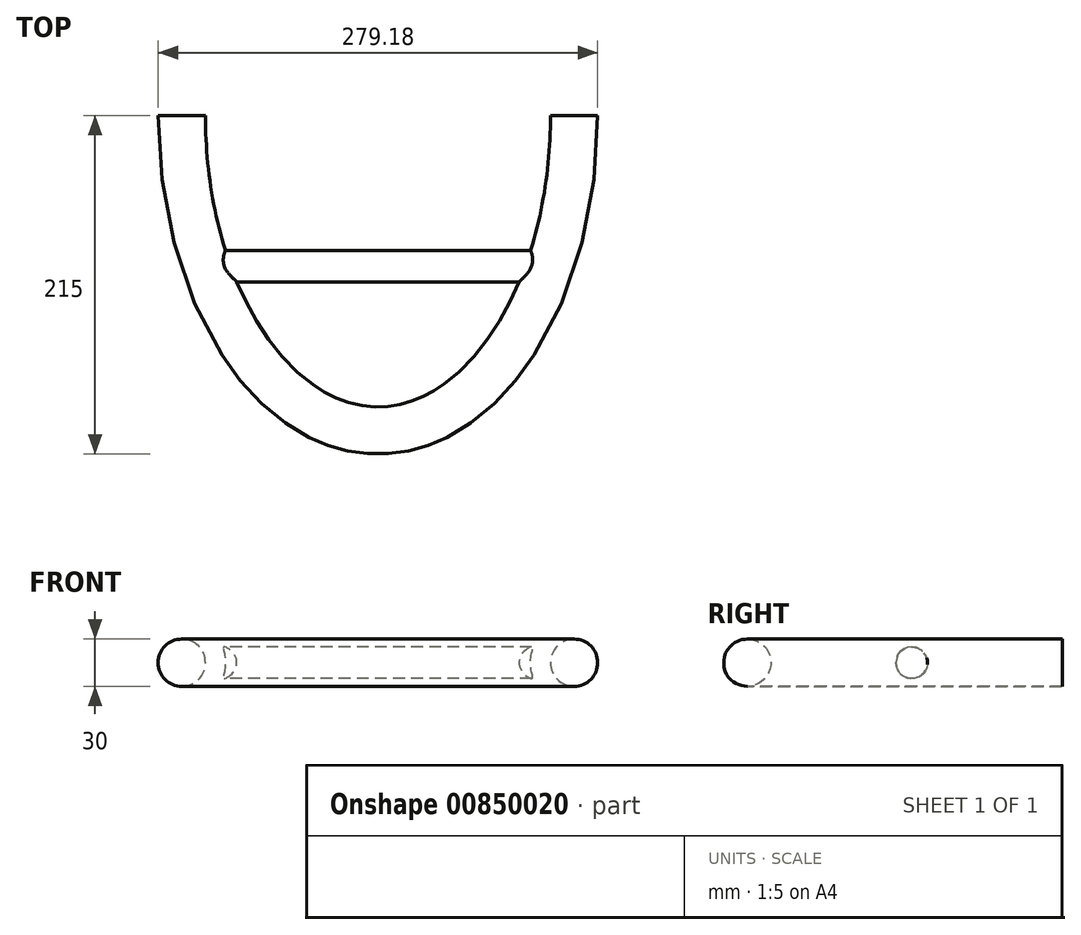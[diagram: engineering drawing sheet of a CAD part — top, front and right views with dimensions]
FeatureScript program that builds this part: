
annotation { "Feature Type Name" : "Feature", "Feature Type Description" : "" }
export const myFeature = defineFeature(function(context is Context, id is Id, definition is map)
    precondition{}
    {
        {
            var Q0;
            Q0=qCreatedBy(makeId("Front.planeOp"),FACE);
            var sketch = newSketch(context, id + "F0", { "sketchPlane" : qUnion([Q0])});
            skCircle(sketch, "E0", {"center": v(0, 0) * mm, "radius": 15 * mm});
            skSolve(sketch);
        }
        {
            var Q0;
            Q0=qCreatedBy(makeId("Top.planeOp"),FACE);
            var sketch = newSketch(context, id + "F1", { "sketchPlane" : qUnion([Q0])});
            skEllipticalArc(sketch, "E1", {});
            skPoint(sketch, "E2.orphan", {"position": v(0, 0) * mm});
            skPoint(sketch, "E3.end.orphan", {"position": v(-249.18, 0) * mm});
            const initialGuessF1  = {"E1": [-0.124588, 0, 0, -1, 0.2, 0.124588, 4.71238898038469, 1.5707963267948966]};
            skSetInitialGuess(sketch, initialGuessF1);
            skSolve(sketch);
        }
        {
            var Q0;
            Q0=makeQuery(id+"F0.imprint","IMPRINT",FACE,{"disambiguationData":[TD([[makeQuery(id+"F0.imprint","IMPRINT",EDGE,{"derivedFrom":sQuery(id+"F0.wireOp",EDGE,"E0")}),1.0]])]});
            var Q1;
            Q1=sQuery(id+"F1.wireOp",EDGE,"u3Ne1ne6-5EJg-UHXM-Y9Kc-ZqsVQWQF4uYl");
            var Q2;
            Q2=sQuery(id+"F1.wireOp",EDGE,"E1");
            sweep(context, id + "F2", {"profiles" : qUnion([Q0]), "path" : qUnion([Q1, Q2])});
        }
        {
            var Q0;
            Q0=qCreatedBy(makeId("Right.planeOp"),FACE);
            cPlane(context, id + "F3", {"entities" : qUnion([Q0]), "cplaneType" : CPlaneType.OFFSET, "offset" : 120 * mm, "oppositeDirection" : true, "width" : 150 * mm, "height" : 150 * mm});
        }
        {
            var Q0;
            Q0=qCreatedBy(id+"F3.planeOp",FACE);
            var sketch = newSketch(context, id + "F4", { "sketchPlane" : qUnion([Q0])});
            skCircle(sketch, "E4", {"center": v(-95.56, 0) * mm, "radius": 10 * mm});
            skSolve(sketch);
        }
        {
            var Q0;
            Q0=makeQuery(id+"F4.imprint","IMPRINT",FACE,{"disambiguationData":[TD([[makeQuery(id+"F4.imprint","IMPRINT",EDGE,{"derivedFrom":sQuery(id+"F4.wireOp",EDGE,"E4")}),1.0]])]});
            extrude(context, id + "F5", {"entities" : qUnion([Q0]), "operationType" : NewBodyOperationType.ADD, "endBound" : BoundingType.SYMMETRIC, "depth" : 228 * mm, "offsetDistance" : 25 * mm});
        }
    });
